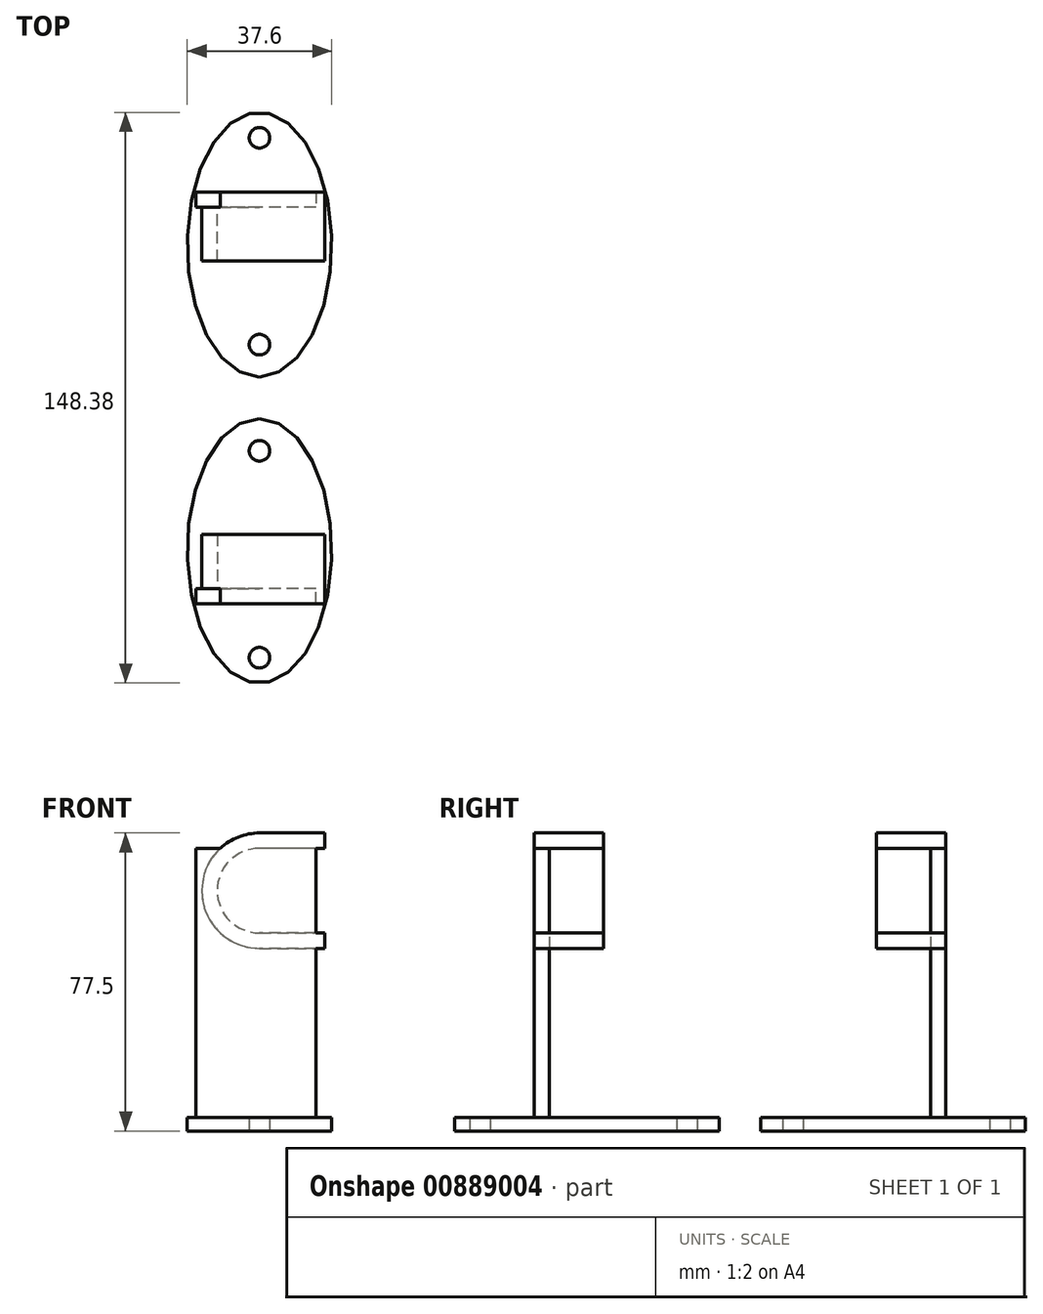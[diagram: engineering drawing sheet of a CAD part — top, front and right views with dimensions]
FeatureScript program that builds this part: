
annotation { "Feature Type Name" : "Feature", "Feature Type Description" : "" }
export const myFeature = defineFeature(function(context is Context, id is Id, definition is map)
    precondition{}
    {
        {
            var Q0;
            Q0=qCreatedBy(makeId("Top.planeOp"),FACE);
            var sketch = newSketch(context, id + "F0", { "sketchPlane" : qUnion([Q0])});
            skEllipse(sketch, "E0", {"center": v(0, 0) * mm, "majorRadius": 34.39 * mm, "minorRadius": 18.8 * mm, "majorAxis": v(0, -1)});
            skLineSegment(sketch, "E1", {"start": v(7.88, 14.48) * mm, "end": v(7.88, -15.14) * mm});
            skLineSegment(sketch, "E2", {"start": v(7.88, 7.82) * mm, "end": v(-6.68, 7.82) * mm});
            skLineSegment(sketch, "E3", {"start": v(-6.68, 7.82) * mm, "end": v(-6.68, -15.14) * mm});
            skLineSegment(sketch, "E4", {"start": v(7.88, -15.14) * mm, "end": v(-6.68, -15.14) * mm});
            skCircle(sketch, "E5", {"center": v(0, 27.8) * mm, "radius": 2.67 * mm});
            skCircle(sketch, "E6", {"center": v(0, -26) * mm, "radius": 2.67 * mm});
            skSolve(sketch);
        }
        {
            var Q0;
            Q0=makeQuery(id+"F0.imprint","IMPRINT",FACE,{"disambiguationData":[TD([[makeQuery(id+"F0.imprint","IMPRINT",EDGE,{"derivedFrom":sQuery(id+"F0.wireOp",EDGE,"E0")}),1.0]])]});
            var Q1;
            {var subQ2=sQuery(id+"F0.wireOp",EDGE,"E2");Q1=makeQuery(id+"F0.imprint","IMPRINT",FACE,{"disambiguationData":[TD([[makeQuery(id+"F0.imprint","IMPRINT",EDGE,{"derivedFrom":subQ2}),1.0]])]});}
            extrude(context, id + "F1", {"entities" : qUnion([Q0, Q1]), "depth" : 3.5 * mm, "offsetDistance" : 25 * mm});
        }
        {
            var Q0;
            Q0=makeQuery(id+"F1.opExtrude","CAP_FACE",FACE,{"disambiguationData":[OSD([sQuery(id+"F0.wireOp",EDGE,"E0"),sQuery(id+"F0.wireOp",EDGE,"E5"),sQuery(id+"F0.wireOp",EDGE,"E6")])],"isStart":false});
            var sketch = newSketch(context, id + "F2", { "sketchPlane" : qUnion([Q0])});
            skLineSegment(sketch, "E7.bottom", {"start": v(14.7, 13.74) * mm, "end": v(-16.57, 13.74) * mm});
            skLineSegment(sketch, "E7.top", {"start": v(14.7, 9.79) * mm, "end": v(-16.57, 9.79) * mm});
            skLineSegment(sketch, "E7.left", {"start": v(14.7, 13.74) * mm, "end": v(14.7, 9.79) * mm});
            skLineSegment(sketch, "E7.right", {"start": v(-16.57, 13.74) * mm, "end": v(-16.57, 9.79) * mm});
            skSolve(sketch);
        }
        {
            var Q0;
            Q0=makeQuery(id+"F2.imprint","IMPRINT",FACE,{"disambiguationData":[TD([[makeQuery(id+"F2.imprint","IMPRINT",EDGE,{"derivedFrom":sQuery(id+"F2.wireOp",EDGE,"E7.bottom")}),1.0]])]});
            extrude(context, id + "F3", {"entities" : qUnion([Q0]), "operationType" : NewBodyOperationType.ADD, "depth" : 70 * mm, "offsetDistance" : 25 * mm});
        }
        {
            var Q0;
            Q0=makeQuery(id+"F3.opExtrude","SWEPT_FACE",FACE,{"disambiguationData":[OSD([sQuery(id+"F2.wireOp",EDGE,"E7.bottom")])]});
            var sketch = newSketch(context, id + "F4", { "sketchPlane" : qUnion([Q0])});
            skCircle(sketch, "E8", {"center": v(0, 62.5) * mm, "radius": 11 * mm});
            skCircle(sketch, "E9.0", {"center": v(0, 62.5) * mm, "radius": 15 * mm});
            skLineSegment(sketch, "E10", {"start": v(0, 51.5) * mm, "end": v(-46.9, 51.5) * mm});
            skLineSegment(sketch, "E11", {"start": v(0.94, 73.5) * mm, "end": v(-53.76, 73.5) * mm});
            skLineSegment(sketch, "E12", {"start": v(0, 47.5) * mm, "end": v(-46.9, 47.5) * mm});
            skLineSegment(sketch, "E13", {"start": v(0, 77.5) * mm, "end": v(-53.76, 77.5) * mm});
            skLineSegment(sketch, "E14", {"start": v(-46.9, 51.5) * mm, "end": v(-46.9, 47.5) * mm});
            skLineSegment(sketch, "E15", {"start": v(-53.76, 73.5) * mm, "end": v(-53.76, 77.5) * mm});
            skLineSegment(sketch, "E16", {"start": v(-17, 47.5) * mm, "end": v(-17, 77.5) * mm});
            skSolve(sketch);
        }
        {
            var Q0;
            {var subQ1=sQuery(id+"F4.wireOp",EDGE,"E9.0");var subQ6=makeQuery(id+"F4.imprint","INTERSECT",VERTEX,{"derivedFrom":[subQ1,sQuery(id+"F4.wireOp",EDGE,"E13")]});Q0=makeQuery(id+"F4.imprint","IMPRINT",FACE,{"disambiguationData":[TD([[makeQuery(id+"F4.imprint","IMPRINT",EDGE,{"disambiguationData":[TD([[subQ6,-1.0]])],"derivedFrom":subQ1}),1.0]])]});}
            var Q1;
            {var subQ0=sQuery(id+"F4.wireOp",EDGE,"E13");var subQ1=sQuery(id+"F4.wireOp",EDGE,"E9.0");var subQ2=makeQuery(id+"F4.imprint","INTERSECT",VERTEX,{"derivedFrom":[subQ1,subQ0]});Q1=makeQuery(id+"F4.imprint","IMPRINT",FACE,{"disambiguationData":[TD([[makeQuery(id+"F4.imprint","IMPRINT",EDGE,{"disambiguationData":[TD([[subQ2,-1.0]])],"derivedFrom":subQ1}),-1.0]])]});}
            var Q2;
            {var subQ0=sQuery(id+"F4.wireOp",EDGE,"E16");var subQ5=sQuery(id+"F4.wireOp",EDGE,"E12");var subQ7=makeQuery(id+"F4.imprint","INTERSECT",VERTEX,{"derivedFrom":[subQ5,subQ0]});Q2=makeQuery(id+"F4.imprint","IMPRINT",FACE,{"disambiguationData":[TD([[makeQuery(id+"F4.imprint","IMPRINT",EDGE,{"disambiguationData":[TD([[subQ7,-1.0]])],"derivedFrom":subQ0}),-1.0]])]});}
            var Q3;
            {var subQ0=sQuery(id+"F4.wireOp",EDGE,"E12");var subQ1=sQuery(id+"F4.wireOp",EDGE,"E9.0");var subQ2=makeQuery(id+"F4.imprint","INTERSECT",VERTEX,{"derivedFrom":[subQ1,subQ0]});Q3=makeQuery(id+"F4.imprint","IMPRINT",FACE,{"disambiguationData":[TD([[makeQuery(id+"F4.imprint","IMPRINT",EDGE,{"disambiguationData":[TD([[subQ2,1.0]])],"derivedFrom":subQ1}),-1.0]])]});}
            var Q4;
            {var subQ0=sQuery(id+"F4.wireOp",EDGE,"E10");var subQ1=sQuery(id+"F4.wireOp",EDGE,"E8");var subQ2=makeQuery(id+"F4.imprint","INTERSECT",VERTEX,{"derivedFrom":[subQ1,subQ0]});Q4=makeQuery(id+"F4.imprint","IMPRINT",FACE,{"disambiguationData":[TD([[makeQuery(id+"F4.imprint","IMPRINT",EDGE,{"disambiguationData":[TD([[subQ2,-1.0]])],"derivedFrom":subQ1}),-1.0]])]});}
            extrude(context, id + "F5", {"entities" : qUnion([Q0, Q1, Q2, Q3, Q4]), "operationType" : NewBodyOperationType.ADD, "oppositeDirection" : true, "depth" : 18 * mm, "offsetDistance" : 25 * mm});
        }
        {
            var Q0;
            Q0=qCreatedBy(makeId("Front.planeOp"),FACE);
            cPlane(context, id + "F6", {"entities" : qUnion([Q0]), "cplaneType" : CPlaneType.OFFSET, "offset" : 39.8 * mm, "width" : 150 * mm, "height" : 150 * mm});
        }
        {
            var Q0;
            Q0=makeQuery(id+"F1.opExtrude","SWEPT_BODY",BODY,{"disambiguationData":[OSD([sQuery(id+"F0.wireOp",EDGE,"E0"),sQuery(id+"F0.wireOp",EDGE,"E5"),sQuery(id+"F0.wireOp",EDGE,"E6")])]});
            var Q1;
            Q1=qCreatedBy(id+"F6.planeOp",FACE);
            mirror(context, id + "F7", {"entities" : qUnion([Q0]), "mirrorPlane" : qUnion([Q1])});
        }
    });
